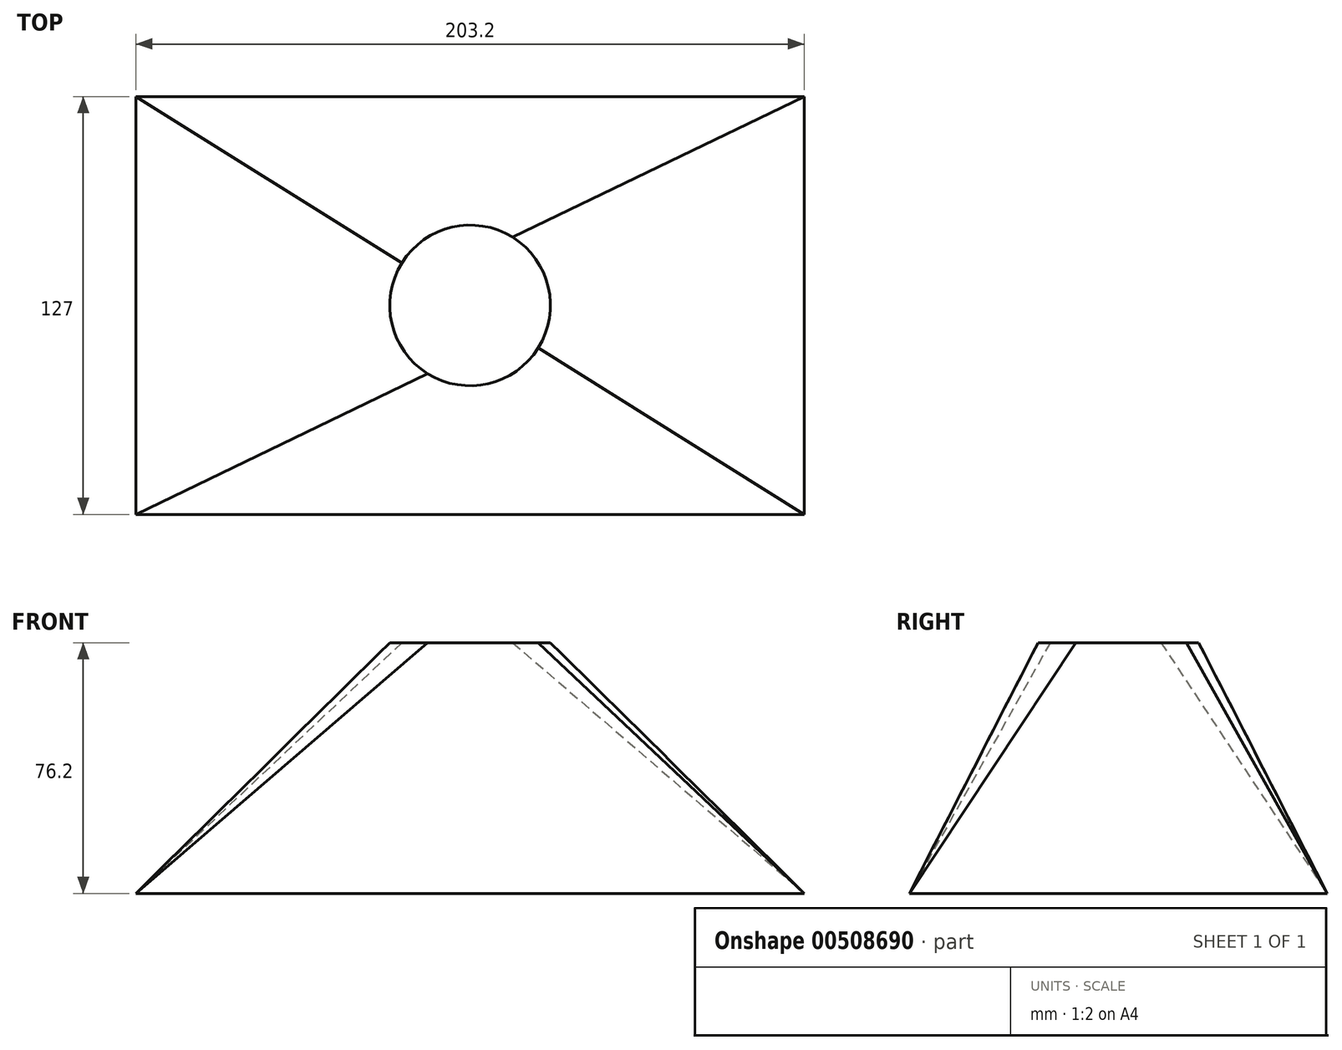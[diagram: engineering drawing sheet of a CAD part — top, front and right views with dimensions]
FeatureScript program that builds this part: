
annotation { "Feature Type Name" : "Feature", "Feature Type Description" : "" }
export const myFeature = defineFeature(function(context is Context, id is Id, definition is map)
    precondition{}
    {
        {
            var Q0;
            Q0=qCreatedBy(makeId("Top.planeOp"),FACE);
            var sketch = newSketch(context, id + "F0", { "sketchPlane" : qUnion([Q0])});
            skLineSegment(sketch, "E0.bottom", {"start": v(-101.6, 63.5) * mm, "end": v(101.6, 63.5) * mm});
            skLineSegment(sketch, "E0.top", {"start": v(-101.6, -63.5) * mm, "end": v(101.6, -63.5) * mm});
            skLineSegment(sketch, "E0.left", {"start": v(-101.6, 63.5) * mm, "end": v(-101.6, -63.5) * mm});
            skLineSegment(sketch, "E0.right", {"start": v(101.6, 63.5) * mm, "end": v(101.6, -63.5) * mm});
            skPoint(sketch, "E0.middle", {"position": v(0, 0) * mm});
            skSolve(sketch);
        }
        {
            var Q0;
            Q0=qCreatedBy(makeId("Top.planeOp"),FACE);
            cPlane(context, id + "F1", {"entities" : qUnion([Q0]), "cplaneType" : CPlaneType.OFFSET, "offset" : 76.2 * mm, "width" : 152.4 * mm, "height" : 152.4 * mm});
        }
        {
            var Q0;
            Q0=qCreatedBy(id+"F1.planeOp",FACE);
            var sketch = newSketch(context, id + "F2", { "sketchPlane" : qUnion([Q0])});
            skCircle(sketch, "E1", {"center": v(0, 0) * mm, "radius": 24.42 * mm});
            skSolve(sketch);
        }
        {
            var Q0;
            Q0=makeQuery(id+"F2.imprint","IMPRINT",FACE,{"disambiguationData":[TD([[makeQuery(id+"F2.imprint","IMPRINT",EDGE,{"derivedFrom":sQuery(id+"F2.wireOp",EDGE,"E1")}),1.0]])]});
            var Q1;
            Q1=makeQuery(id+"F0.imprint","IMPRINT",FACE,{"disambiguationData":[TD([[makeQuery(id+"F0.imprint","IMPRINT",EDGE,{"derivedFrom":sQuery(id+"F0.wireOp",EDGE,"E0.bottom")}),-1.0]])]});
            loft(context, id + "F3", {"sheetProfilesArray" : [{ "sheetProfileEntities" : qUnion([Q0]) }, { "sheetProfileEntities" : qUnion([Q1]) }]});
        }
    });
